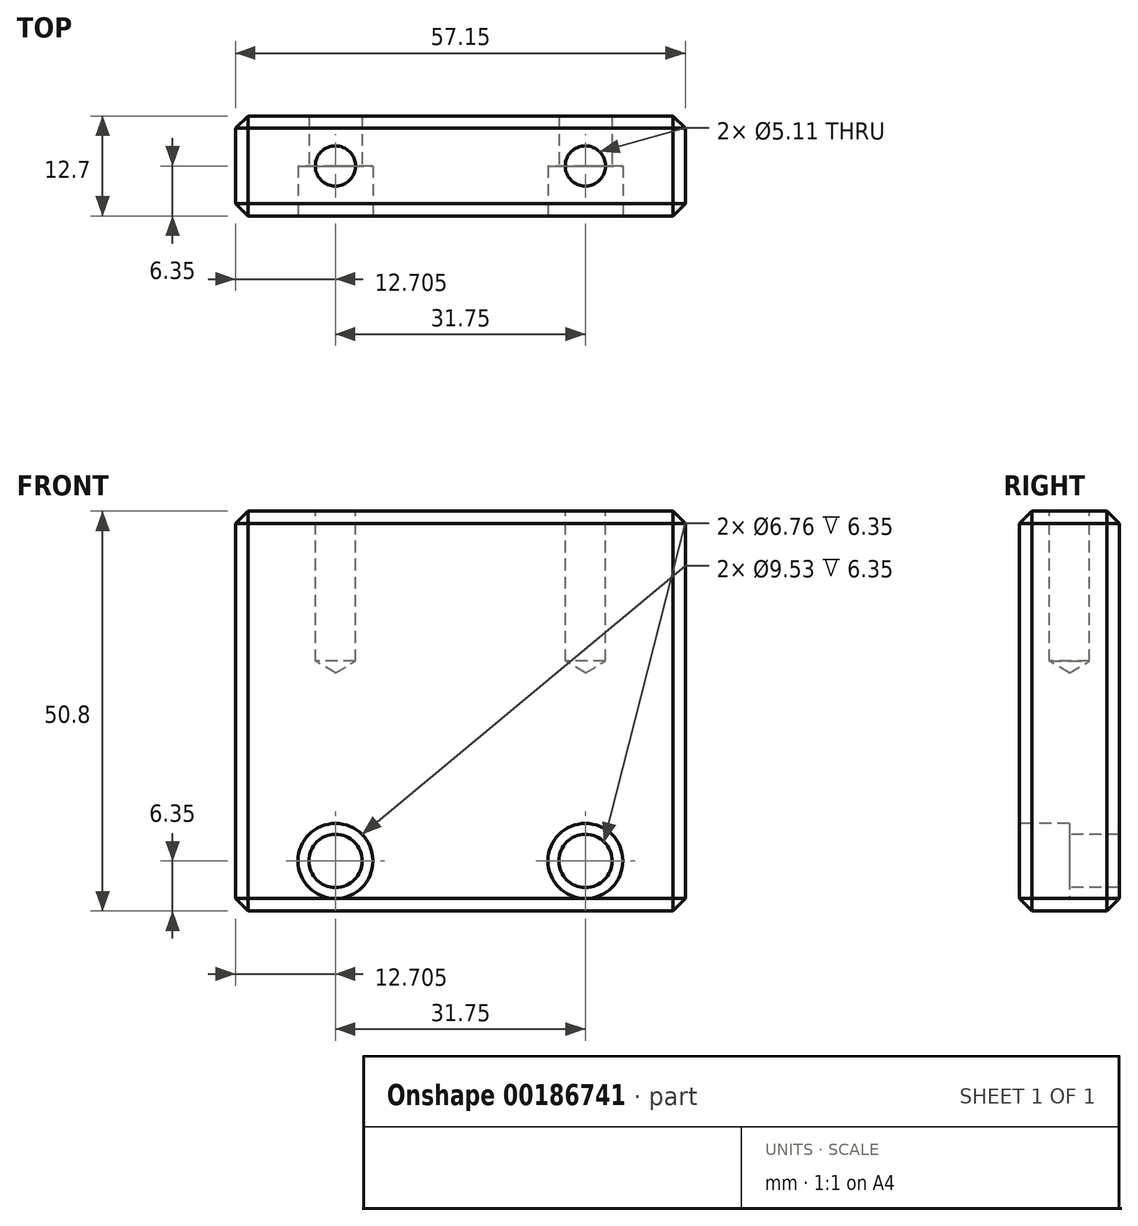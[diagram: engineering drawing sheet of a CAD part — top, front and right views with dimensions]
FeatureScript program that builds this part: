
annotation { "Feature Type Name" : "Feature", "Feature Type Description" : "" }
export const myFeature = defineFeature(function(context is Context, id is Id, definition is map)
    precondition{}
    {
        {
            var Q0;
            Q0=qCreatedBy(makeId("Front.planeOp"),FACE);
            var sketch = newSketch(context, id + "F0", { "sketchPlane" : qUnion([Q0])});
            skLineSegment(sketch, "E0.bottom", {"start": v(28.58, 25.4) * mm, "end": v(-28.57, 25.4) * mm});
            skLineSegment(sketch, "E0.top", {"start": v(28.58, -25.4) * mm, "end": v(-28.58, -25.4) * mm});
            skLineSegment(sketch, "E0.left", {"start": v(28.58, 25.4) * mm, "end": v(28.58, -25.4) * mm});
            skLineSegment(sketch, "E0.right", {"start": v(-28.57, 25.4) * mm, "end": v(-28.58, -25.4) * mm});
            skPoint(sketch, "E0.middle", {"position": v(0, 0) * mm});
            skPoint(sketch, "E1", {"position": v(-15.88, -19.05) * mm});
            skPoint(sketch, "E2.MirrorP", {"position": v(15.88, -19.05) * mm});
            skPoint(sketch, "E3.MirrorP", {"position": v(-15.88, 19.05) * mm});
            skPoint(sketch, "E4.MirrorP", {"position": v(15.88, 19.05) * mm});
            skSolve(sketch);
        }
        {
            var Q0;
            Q0=makeQuery(id+"F0.imprint","IMPRINT",FACE,{"disambiguationData":[TD([[makeQuery(id+"F0.imprint","IMPRINT",EDGE,{"derivedFrom":sQuery(id+"F0.wireOp",EDGE,"E0.bottom")}),1.0]])]});
            extrude(context, id + "F1", {"entities" : qUnion([Q0]), "oppositeDirection" : true, "depth" : 12.7 * mm});
        }
        {
            var Q0;
            Q0=sQuery(id+"F0.wireOp",VERTEX,"E3.MirrorP");
            var Q1;
            Q1=sQuery(id+"F0.wireOp",VERTEX,"E4.MirrorP");
            var Q2;
            Q2=makeQuery(id+"F1.opExtrude","SWEPT_BODY",BODY,{"disambiguationData":[OSD([sQuery(id+"F0.wireOp",EDGE,"E0.bottom"),sQuery(id+"F0.wireOp",EDGE,"E0.top"),sQuery(id+"F0.wireOp",EDGE,"E0.left"),sQuery(id+"F0.wireOp",EDGE,"E0.right")])]});
            hole(context, id + "F2", {"style" : HoleStyle.C_BORE, "endStyle" : HoleEndStyle.THROUGH, "holeDiameter" : 6.76 * mm, "cBoreDiameter" : 9.52 * mm, "cBoreDepth" : 6.35 * mm, "startFromSketch" : true, "locations" : qUnion([Q0, Q1]), "scope" : qUnion([Q2]), "isTappedThrough" : true});
        }
        {
            var Q0;
            Q0=makeQuery(id+"F1.opExtrude","SWEPT_FACE",FACE,{"disambiguationData":[OSD([sQuery(id+"F0.wireOp",EDGE,"E0.top")])]});
            var sketch = newSketch(context, id + "F3", { "sketchPlane" : qUnion([Q0])});
            skPoint(sketch, "E5", {"position": v(-15.88, -6.35) * mm});
            skPoint(sketch, "E6.MirrorP", {"position": v(15.88, -6.35) * mm});
            skSolve(sketch);
        }
        {
            var Q0;
            Q0=sQuery(id+"F3.wireOp",VERTEX,"E6.MirrorP");
            var Q1;
            Q1=sQuery(id+"F3.wireOp",VERTEX,"E5");
            var Q2;
            Q2=makeQuery(id+"F1.opExtrude","SWEPT_BODY",BODY,{"disambiguationData":[OSD([sQuery(id+"F0.wireOp",EDGE,"E0.bottom"),sQuery(id+"F0.wireOp",EDGE,"E0.top"),sQuery(id+"F0.wireOp",EDGE,"E0.left"),sQuery(id+"F0.wireOp",EDGE,"E0.right")])]});
            hole(context, id + "F4", {"style" : HoleStyle.SIMPLE, "endStyle" : HoleEndStyle.BLIND, "standardTappedOrClearance" : lookupTablePath({ "standard" : "ANSI", "engagement" : "75%", "pitch" : "20 tpi", "size" : "1/4", "type" : "Tapped" }), "standardBlindInLast" : lookupTablePath({ "standard" : "ANSI", "engagement" : "75%", "pitch" : "20 tpi", "size" : "1/4", "type" : "Tapped" }), "holeDiameter" : 5.1 * mm, "holeDepth" : 19.05 * mm, "startFromSketch" : true, "locations" : qUnion([Q0, Q1]), "scope" : qUnion([Q2]), "majorDiameter" : 6.35 * mm});
        }
        {
            var Q0;
            Q0=makeQuery(id+"F1.opExtrude","CAP_EDGE",EDGE,{"disambiguationData":[OSD([sQuery(id+"F0.wireOp",EDGE,"E0.left")])],"isStart":false});
            var Q1;
            Q1=makeQuery(id+"F1.opExtrude","CAP_EDGE",EDGE,{"disambiguationData":[OSD([sQuery(id+"F0.wireOp",EDGE,"E0.left")])],"isStart":true});
            var Q2;
            Q2=makeQuery(id+"F1.opExtrude","CAP_EDGE",EDGE,{"disambiguationData":[OSD([sQuery(id+"F0.wireOp",EDGE,"E0.right")])],"isStart":true});
            var Q3;
            Q3=makeQuery(id+"F1.opExtrude","CAP_EDGE",EDGE,{"disambiguationData":[OSD([sQuery(id+"F0.wireOp",EDGE,"E0.right")])],"isStart":false});
            var Q4;
            Q4=makeQuery(id+"F1.opExtrude","CAP_EDGE",EDGE,{"disambiguationData":[OSD([sQuery(id+"F0.wireOp",EDGE,"E0.top")])],"isStart":true});
            var Q5;
            Q5=makeQuery(id+"F1.opExtrude","SWEPT_EDGE",EDGE,{"disambiguationData":[OSD([sQuery(id+"F0.wireOp",EDGE,"E0.top"),sQuery(id+"F0.wireOp",EDGE,"E0.right")])]});
            var Q6;
            Q6=makeQuery(id+"F1.opExtrude","CAP_EDGE",EDGE,{"disambiguationData":[OSD([sQuery(id+"F0.wireOp",EDGE,"E0.top")])],"isStart":false});
            var Q7;
            Q7=makeQuery(id+"F1.opExtrude","SWEPT_EDGE",EDGE,{"disambiguationData":[OSD([sQuery(id+"F0.wireOp",EDGE,"E0.top"),sQuery(id+"F0.wireOp",EDGE,"E0.left")])]});
            var Q8;
            Q8=makeQuery(id+"F1.opExtrude","SWEPT_FACE",FACE,{"disambiguationData":[OSD([sQuery(id+"F0.wireOp",EDGE,"E0.bottom")])]});
            chamfer(context, id + "F5", {"entities" : qUnion([Q0, Q1, Q2, Q3, Q4, Q5, Q6, Q7, Q8]), "width" : 1.57 * mm, "tangentPropagation" : true});
        }
        {
            var Q0;
            Q0=makeQuery(id+"F1.opExtrude","SWEPT_BODY",BODY,{"disambiguationData":[OSD([sQuery(id+"F0.wireOp",EDGE,"E0.bottom"),sQuery(id+"F0.wireOp",EDGE,"E0.top"),sQuery(id+"F0.wireOp",EDGE,"E0.left"),sQuery(id+"F0.wireOp",EDGE,"E0.right")])]});
            var Q1;
            {var subQ0=sQuery(id+"F0.wireOp",EDGE,"E0.left");Q1=makeQuery(id+"F5.opChamfer","BLEND_EDGE",EDGE,{"blendedFrom":[makeQuery(id+"F1.opExtrude","SWEPT_EDGE",EDGE,{"disambiguationData":[OSD([sQuery(id+"F0.wireOp",EDGE,"E0.bottom"),subQ0])]}),makeQuery(id+"F1.opExtrude","SWEPT_FACE",FACE,{"disambiguationData":[OSD([subQ0])]})],"blendedInto":[makeQuery(id+"F1.opExtrude","SWEPT_FACE",FACE,{"disambiguationData":[OSD([subQ0])]})]});}
            transform(context, id + "F6", {"entities" : qUnion([Q0]), "transformType" : TransformType.ROTATION, "transformAxis" : qUnion([Q1]), "angle" : 180 * degree, "makeCopy" : false});
        }
    });
